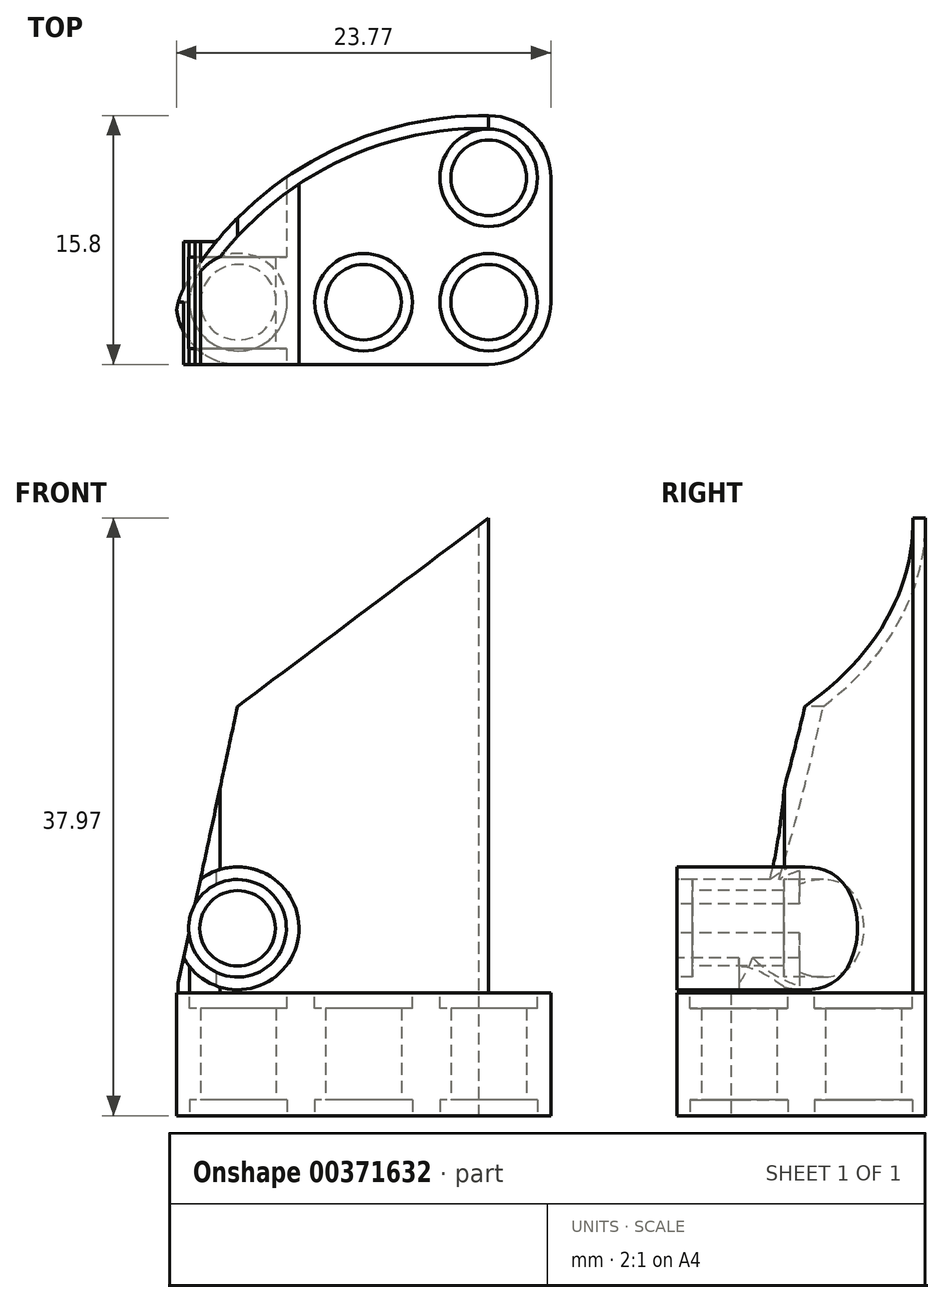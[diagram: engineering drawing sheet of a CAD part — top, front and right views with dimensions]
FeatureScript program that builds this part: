
annotation { "Feature Type Name" : "Feature", "Feature Type Description" : "" }
export const myFeature = defineFeature(function(context is Context, id is Id, definition is map)
    precondition{}
    {
        {
            var Q0;
            Q0=qCreatedBy(makeId("Top.planeOp"),FACE);
            var sketch = newSketch(context, id + "F0", { "sketchPlane" : qUnion([Q0])});
            skLineSegment(sketch, "E0", {"start": v(0, 0) * mm, "end": v(11.9, 0) * mm, "construction": true});
            skLineSegment(sketch, "E1", {"start": v(11.9, 0) * mm, "end": v(11.9, 7.9) * mm});
            skLineSegment(sketch, "E2", {"start": v(11.9, 0) * mm, "end": v(11.9, -7.9) * mm});
            skLineSegment(sketch, "E3", {"start": v(11.9, -7.9) * mm, "end": v(-11.9, -7.9) * mm});
            skLineSegment(sketch, "E4", {"start": v(-11.9, -7.9) * mm, "end": v(-11.9, 0) * mm});
            skLineSegment(sketch, "E5", {"start": v(11.9, 7.9) * mm, "end": v(4, 7.9) * mm});
            skLineSegment(sketch, "E6", {"start": v(4, 7.9) * mm, "end": v(4, 0) * mm});
            skLineSegment(sketch, "E7", {"start": v(4, 0) * mm, "end": v(-11.9, 0) * mm});
            skCircle(sketch, "E8", {"center": v(7.95, 3.95) * mm, "radius": 2.4 * mm});
            skPoint(sketch, "E8.centerSnap0", {"position": v(7.95, 7.9) * mm});
            skPoint(sketch, "E8.centerSnap1", {"position": v(11.9, 3.95) * mm});
            skCircle(sketch, "E9", {"center": v(7.95, 3.95) * mm, "radius": 3.1 * mm});
            skLineSegment(sketch, "E10", {"start": v(11.9, -7.9) * mm, "end": v(4, -7.9) * mm, "construction": true});
            skLineSegment(sketch, "E11", {"start": v(4, -7.9) * mm, "end": v(-4, -7.9) * mm, "construction": true});
            skLineSegment(sketch, "E12", {"start": v(-4, -7.9) * mm, "end": v(-11.9, -7.9) * mm, "construction": true});
            skLineSegment(sketch, "E13", {"start": v(11.9, -3.95) * mm, "end": v(-11.9, -3.95) * mm, "construction": true});
            skCircle(sketch, "E14", {"center": v(7.95, -3.95) * mm, "radius": 2.4 * mm});
            skPoint(sketch, "E14.centerSnap0", {"position": v(7.95, -7.9) * mm});
            skCircle(sketch, "E15", {"center": v(7.95, -3.95) * mm, "radius": 3.1 * mm});
            skCircle(sketch, "E16", {"center": v(0, -3.95) * mm, "radius": 2.4 * mm});
            skCircle(sketch, "E17", {"center": v(0, -3.95) * mm, "radius": 3.1 * mm});
            skCircle(sketch, "E18", {"center": v(-7.95, -3.95) * mm, "radius": 2.4 * mm});
            skPoint(sketch, "E18.centerSnap0", {"position": v(-7.95, -7.9) * mm});
            skCircle(sketch, "E19", {"center": v(-7.95, -3.95) * mm, "radius": 3.1 * mm});
            skArc(sketch, "E20", {"start": v(7.95, 7.9) * mm, "mid": v(-3.66, 4.8) * mm, "end": v(-11.9, -3.95) * mm});
            skArc(sketch, "E21.trimOffspring", {"start": v(-10.35, -3.82) * mm, "mid": v(-10.38, -3.88) * mm, "end": v(-10.42, -3.95) * mm});
            skArc(sketch, "E22.0", {"start": v(7.94, 7.1) * mm, "mid": v(-1.55, 5.02) * mm, "end": v(-9.1, -1.07) * mm});
            skLineSegment(sketch, "E23", {"start": v(7.95, 7.9) * mm, "end": v(7.94, 7.1) * mm});
            skLineSegment(sketch, "E24", {"start": v(-11.9, -3.95) * mm, "end": v(-11.05, -3.95) * mm});
            skArc(sketch, "E25.trimOffspring", {"start": v(-11, -3.95) * mm, "mid": v(-11.02, -4) * mm, "end": v(-11.05, -4.05) * mm});
            skSolve(sketch);
        }
        {
            var Q0;
            Q0=makeQuery(id+"F0.imprint","IMPRINT",FACE,{"disambiguationData":[TD([[makeQuery(id+"F0.imprint","IMPRINT",EDGE,{"derivedFrom":sQuery(id+"F0.wireOp",EDGE,"E1")}),1.0]])]});
            var Q1;
            Q1=makeQuery(id+"F0.imprint","IMPRINT",FACE,{"disambiguationData":[TD([[makeQuery(id+"F0.imprint","IMPRINT",EDGE,{"derivedFrom":sQuery(id+"F0.wireOp",EDGE,"E14")}),-1.0]])]});
            var Q2;
            Q2=makeQuery(id+"F0.imprint","IMPRINT",FACE,{"disambiguationData":[TD([[makeQuery(id+"F0.imprint","IMPRINT",EDGE,{"derivedFrom":sQuery(id+"F0.wireOp",EDGE,"E8")}),-1.0]])]});
            var Q3;
            Q3=makeQuery(id+"F0.imprint","IMPRINT",FACE,{"disambiguationData":[TD([[makeQuery(id+"F0.imprint","IMPRINT",EDGE,{"derivedFrom":sQuery(id+"F0.wireOp",EDGE,"E16")}),-1.0]])]});
            var Q4;
            Q4=makeQuery(id+"F0.imprint","IMPRINT",FACE,{"disambiguationData":[TD([[makeQuery(id+"F0.imprint","IMPRINT",EDGE,{"derivedFrom":sQuery(id+"F0.wireOp",EDGE,"E18")}),-1.0]])]});
            extrude(context, id + "F1", {"entities" : qUnion([Q0, Q1, Q2, Q3, Q4]), "depth" : 7.8 * mm});
        }
        {
            var Q0;
            Q0=makeQuery(id+"F0.imprint","IMPRINT",FACE,{"disambiguationData":[TD([[makeQuery(id+"F0.imprint","IMPRINT",EDGE,{"derivedFrom":sQuery(id+"F0.wireOp",EDGE,"E8")}),-1.0]])]});
            var Q1;
            Q1=makeQuery(id+"F0.imprint","IMPRINT",FACE,{"disambiguationData":[TD([[makeQuery(id+"F0.imprint","IMPRINT",EDGE,{"derivedFrom":sQuery(id+"F0.wireOp",EDGE,"E14")}),-1.0]])]});
            var Q2;
            Q2=makeQuery(id+"F0.imprint","IMPRINT",FACE,{"disambiguationData":[TD([[makeQuery(id+"F0.imprint","IMPRINT",EDGE,{"derivedFrom":sQuery(id+"F0.wireOp",EDGE,"E16")}),-1.0]])]});
            var Q3;
            Q3=makeQuery(id+"F0.imprint","IMPRINT",FACE,{"disambiguationData":[TD([[makeQuery(id+"F0.imprint","IMPRINT",EDGE,{"derivedFrom":sQuery(id+"F0.wireOp",EDGE,"E18")}),-1.0]])]});
            extrude(context, id + "F2", {"entities" : qUnion([Q0, Q1, Q2, Q3]), "operationType" : NewBodyOperationType.REMOVE, "depth" : 1 * mm});
        }
        {
            var Q0;
            Q0=makeQuery(id+"F1.opExtrude","CAP_FACE",FACE,{"disambiguationData":[OSD([sQuery(id+"F0.wireOp",EDGE,"E1"),sQuery(id+"F0.wireOp",EDGE,"E2"),sQuery(id+"F0.wireOp",EDGE,"E3"),sQuery(id+"F0.wireOp",EDGE,"E4"),sQuery(id+"F0.wireOp",EDGE,"E5"),sQuery(id+"F0.wireOp",EDGE,"E6"),sQuery(id+"F0.wireOp",EDGE,"E7"),sQuery(id+"F0.wireOp",EDGE,"E8"),sQuery(id+"F0.wireOp",EDGE,"E14"),sQuery(id+"F0.wireOp",EDGE,"E16"),sQuery(id+"F0.wireOp",EDGE,"E18")])],"isStart":false});
            var sketch = newSketch(context, id + "F3", { "sketchPlane" : qUnion([Q0])});
            skCircle(sketch, "E26", {"center": v(7.95, 3.95) * mm, "radius": 3.1 * mm});
            skCircle(sketch, "E27", {"center": v(7.95, -3.95) * mm, "radius": 3.1 * mm});
            skCircle(sketch, "E28", {"center": v(0, -3.95) * mm, "radius": 3.1 * mm});
            skCircle(sketch, "E29", {"center": v(-7.95, -3.95) * mm, "radius": 3.1 * mm});
            skSolve(sketch);
        }
        {
            var Q0;
            Q0=makeQuery(id+"F3.imprint","IMPRINT",FACE,{"disambiguationData":[TD([[makeQuery(id+"F3.imprint","IMPRINT",EDGE,{"derivedFrom":sQuery(id+"F3.wireOp",EDGE,"E26")}),1.0]])]});
            var Q1;
            Q1=makeQuery(id+"F3.imprint","IMPRINT",FACE,{"disambiguationData":[TD([[makeQuery(id+"F3.imprint","IMPRINT",EDGE,{"derivedFrom":sQuery(id+"F3.wireOp",EDGE,"E27")}),1.0]])]});
            var Q2;
            Q2=makeQuery(id+"F3.imprint","IMPRINT",FACE,{"disambiguationData":[TD([[makeQuery(id+"F3.imprint","IMPRINT",EDGE,{"derivedFrom":sQuery(id+"F3.wireOp",EDGE,"E28")}),1.0]])]});
            var Q3;
            Q3=makeQuery(id+"F3.imprint","IMPRINT",FACE,{"disambiguationData":[TD([[makeQuery(id+"F3.imprint","IMPRINT",EDGE,{"derivedFrom":sQuery(id+"F3.wireOp",EDGE,"E29")}),1.0]])]});
            extrude(context, id + "F4", {"entities" : qUnion([Q0, Q1, Q2, Q3]), "operationType" : NewBodyOperationType.REMOVE, "oppositeDirection" : true, "depth" : 1 * mm});
        }
        {
            var Q0;
            {var subQ5=sQuery(id+"F0.wireOp",EDGE,"E24");Q0=makeQuery(id+"F0.imprint","IMPRINT",FACE,{"disambiguationData":[TD([[makeQuery(id+"F0.imprint","IMPRINT",EDGE,{"derivedFrom":subQ5}),1.0]])]});}
            var Q1;
            {var subQ0=sQuery(id+"F0.wireOp",EDGE,"E20");var subQ1=sQuery(id+"F0.wireOp",EDGE,"E6");var subQ2=makeQuery(id+"F0.imprint","INTERSECT",VERTEX,{"derivedFrom":[subQ1,subQ0]});Q1=makeQuery(id+"F0.imprint","IMPRINT",FACE,{"disambiguationData":[TD([[makeQuery(id+"F0.imprint","IMPRINT",EDGE,{"disambiguationData":[TD([[subQ2,-1.0]])],"derivedFrom":subQ1}),-1.0]])]});}
            var Q2;
            {var subQ0=sQuery(id+"F0.wireOp",EDGE,"E23");Q2=makeQuery(id+"F0.imprint","IMPRINT",FACE,{"disambiguationData":[TD([[makeQuery(id+"F0.imprint","IMPRINT",EDGE,{"derivedFrom":subQ0}),-1.0]])]});}
            extrude(context, id + "F5", {"entities" : qUnion([Q0, Q1, Q2]), "operationType" : NewBodyOperationType.ADD, "depth" : 38 * mm});
        }
        {
            var Q0;
            {var subQ0=sQuery(id+"F0.wireOp",EDGE,"E7");var subQ1=sQuery(id+"F0.wireOp",EDGE,"E6");var subQ2=makeQuery(id+"F0.imprint","INTERSECT",VERTEX,{"derivedFrom":[subQ1,subQ0]});Q0=makeQuery(id+"F0.imprint","IMPRINT",FACE,{"disambiguationData":[TD([[makeQuery(id+"F0.imprint","IMPRINT",EDGE,{"disambiguationData":[TD([[subQ2,1.0]])],"derivedFrom":subQ1}),-1.0]])]});}
            extrude(context, id + "F6", {"entities" : qUnion([Q0]), "operationType" : NewBodyOperationType.ADD, "depth" : 7.8 * mm});
        }
        {
            var Q0;
            Q0=makeQuery(id+"F1.opExtrude","SWEPT_FACE",FACE,{"disambiguationData":[OSD([sQuery(id+"F0.wireOp",EDGE,"E3")])]});
            var sketch = newSketch(context, id + "F7", { "sketchPlane" : qUnion([Q0])});
            skLineSegment(sketch, "E30", {"start": v(-11.9, 0) * mm, "end": v(-8, 0) * mm});
            skLineSegment(sketch, "E31", {"start": v(-8, 0) * mm, "end": v(-8, 11.9) * mm});
            skLineSegment(sketch, "E32", {"start": v(-8, 0) * mm, "end": v(-8, 26) * mm, "construction": true});
            skLineSegment(sketch, "E33", {"start": v(11.9, 0) * mm, "end": v(8, 0) * mm, "construction": true});
            skLineSegment(sketch, "E34", {"start": v(8, 0) * mm, "end": v(8, 38) * mm});
            skLineSegment(sketch, "E35", {"start": v(-11.9, 7.8) * mm, "end": v(-8, 26) * mm});
            skLineSegment(sketch, "E36", {"start": v(-8, 26) * mm, "end": v(8, 38) * mm});
            skCircle(sketch, "E37", {"center": v(-8, 11.9) * mm, "radius": 2.4 * mm});
            skCircle(sketch, "E38", {"center": v(-8, 11.9) * mm, "radius": 3.1 * mm});
            skCircle(sketch, "E39", {"center": v(-8, 11.9) * mm, "radius": 3.9 * mm});
            skLineSegment(sketch, "E40", {"start": v(8, 7.8) * mm, "end": v(11.9, 7.8) * mm});
            skLineSegment(sketch, "E41", {"start": v(11.9, 7.8) * mm, "end": v(11.9, 0) * mm});
            skLineSegment(sketch, "E42", {"start": v(-11.9, 0) * mm, "end": v(-11.9, 7.8) * mm});
            skSolve(sketch);
        }
        {
            var Q0;
            Q0=makeQuery(id+"F7.imprint","IMPRINT",FACE,{"disambiguationData":[TD([[makeQuery(id+"F7.imprint","IMPRINT",EDGE,{"derivedFrom":sQuery(id+"F7.wireOp",EDGE,"E37")}),-1.0]])]});
            var Q1;
            {var subQ0=sQuery(id+"F7.wireOp",EDGE,"E38");var subQ1=sQuery(id+"F7.wireOp",EDGE,"E35");var subQ2=makeQuery(id+"F7.imprint","INTERSECT",VERTEX,{"disambiguationData":[OD(0.0)],"derivedFrom":[subQ1,subQ0]});Q1=makeQuery(id+"F7.imprint","IMPRINT",FACE,{"disambiguationData":[TD([[makeQuery(id+"F7.imprint","IMPRINT",EDGE,{"disambiguationData":[TD([[subQ2,-1.0]])],"derivedFrom":subQ1}),1.0]])]});}
            extrude(context, id + "F8", {"entities" : qUnion([Q0, Q1]), "operationType" : NewBodyOperationType.REMOVE, "oppositeDirection" : true, "depth" : 25 * mm});
        }
        {
            var Q0;
            {var subQ0=sQuery(id+"F7.wireOp",EDGE,"E39");var subQ1=sQuery(id+"F7.wireOp",EDGE,"E35");var subQ2=makeQuery(id+"F7.imprint","INTERSECT",VERTEX,{"disambiguationData":[OD(1.0)],"derivedFrom":[subQ1,subQ0]});Q0=makeQuery(id+"F7.imprint","IMPRINT",FACE,{"disambiguationData":[TD([[makeQuery(id+"F7.imprint","IMPRINT",EDGE,{"disambiguationData":[TD([[subQ2,-1.0]])],"derivedFrom":subQ1}),1.0]])]});}
            var Q1;
            {var subQ0=sQuery(id+"F7.wireOp",EDGE,"E39");var subQ1=sQuery(id+"F7.wireOp",EDGE,"E31");var subQ2=makeQuery(id+"F7.imprint","INTERSECT",VERTEX,{"derivedFrom":[subQ1,subQ0]});Q1=makeQuery(id+"F7.imprint","IMPRINT",FACE,{"disambiguationData":[TD([[makeQuery(id+"F7.imprint","IMPRINT",EDGE,{"disambiguationData":[TD([[subQ2,-1.0]])],"derivedFrom":subQ1}),1.0]])]});}
            var Q2;
            {var subQ0=sQuery(id+"F7.wireOp",EDGE,"E39");var subQ1=sQuery(id+"F7.wireOp",EDGE,"E31");var subQ2=makeQuery(id+"F7.imprint","INTERSECT",VERTEX,{"derivedFrom":[subQ1,subQ0]});Q2=makeQuery(id+"F7.imprint","IMPRINT",FACE,{"disambiguationData":[TD([[makeQuery(id+"F7.imprint","IMPRINT",EDGE,{"disambiguationData":[TD([[subQ2,-1.0]])],"derivedFrom":subQ1}),-1.0]])]});}
            var Q3;
            {var subQ0=sQuery(id+"F7.wireOp",EDGE,"E39");var subQ1=sQuery(id+"F7.wireOp",EDGE,"E35");var subQ2=makeQuery(id+"F7.imprint","INTERSECT",VERTEX,{"disambiguationData":[OD(0.0)],"derivedFrom":[subQ1,subQ0]});Q3=makeQuery(id+"F7.imprint","IMPRINT",FACE,{"disambiguationData":[TD([[makeQuery(id+"F7.imprint","IMPRINT",EDGE,{"disambiguationData":[TD([[subQ2,-1.0]])],"derivedFrom":subQ1}),1.0]])]});}
            var Q4;
            {var subQ0=sQuery(id+"F7.wireOp",EDGE,"E38");var subQ1=sQuery(id+"F7.wireOp",EDGE,"E35");var subQ2=makeQuery(id+"F7.imprint","INTERSECT",VERTEX,{"disambiguationData":[OD(0.0)],"derivedFrom":[subQ1,subQ0]});Q4=makeQuery(id+"F7.imprint","IMPRINT",FACE,{"disambiguationData":[TD([[makeQuery(id+"F7.imprint","IMPRINT",EDGE,{"disambiguationData":[TD([[subQ2,-1.0]])],"derivedFrom":subQ1}),1.0]])]});}
            var Q5;
            Q5=makeQuery(id+"F7.imprint","IMPRINT",FACE,{"disambiguationData":[TD([[makeQuery(id+"F7.imprint","IMPRINT",EDGE,{"derivedFrom":sQuery(id+"F7.wireOp",EDGE,"E37")}),-1.0]])]});
            extrude(context, id + "F9", {"entities" : qUnion([Q0, Q1, Q2, Q3, Q4, Q5]), "operationType" : NewBodyOperationType.ADD, "oppositeDirection" : true, "depth" : 7.8 * mm});
        }
        {
            var Q0;
            Q0=makeQuery(id+"F7.imprint","IMPRINT",FACE,{"disambiguationData":[TD([[makeQuery(id+"F7.imprint","IMPRINT",EDGE,{"derivedFrom":sQuery(id+"F7.wireOp",EDGE,"E37")}),1.0]])]});
            extrude(context, id + "F10", {"entities" : qUnion([Q0]), "operationType" : NewBodyOperationType.REMOVE, "oppositeDirection" : true, "depth" : 25 * mm});
        }
        {
            var Q0;
            Q0=makeQuery(id+"F7.imprint","IMPRINT",FACE,{"disambiguationData":[TD([[makeQuery(id+"F7.imprint","IMPRINT",EDGE,{"derivedFrom":sQuery(id+"F7.wireOp",EDGE,"E37")}),-1.0]])]});
            var Q1;
            {var subQ0=sQuery(id+"F7.wireOp",EDGE,"E38");var subQ1=sQuery(id+"F7.wireOp",EDGE,"E35");var subQ2=makeQuery(id+"F7.imprint","INTERSECT",VERTEX,{"disambiguationData":[OD(0.0)],"derivedFrom":[subQ1,subQ0]});Q1=makeQuery(id+"F7.imprint","IMPRINT",FACE,{"disambiguationData":[TD([[makeQuery(id+"F7.imprint","IMPRINT",EDGE,{"disambiguationData":[TD([[subQ2,-1.0]])],"derivedFrom":subQ1}),1.0]])]});}
            extrude(context, id + "F11", {"entities" : qUnion([Q0, Q1]), "operationType" : NewBodyOperationType.REMOVE, "oppositeDirection" : true, "depth" : 1 * mm});
        }
        {
            var Q0;
            {var subQ0=sQuery(id+"F7.wireOp",EDGE,"E36");Q0=makeQuery(id+"F7.imprint","IMPRINT",FACE,{"disambiguationData":[TD([[makeQuery(id+"F7.imprint","IMPRINT",EDGE,{"derivedFrom":subQ0}),-1.0]])]});}
            var Q1;
            {var subQ0=sQuery(id+"F7.wireOp",EDGE,"E39");var subQ1=sQuery(id+"F7.wireOp",EDGE,"E31");var subQ2=makeQuery(id+"F7.imprint","INTERSECT",VERTEX,{"derivedFrom":[subQ1,subQ0]});Q1=makeQuery(id+"F7.imprint","IMPRINT",FACE,{"disambiguationData":[TD([[makeQuery(id+"F7.imprint","IMPRINT",EDGE,{"disambiguationData":[TD([[subQ2,1.0]])],"derivedFrom":subQ1}),1.0]])]});}
            var Q2;
            {var subQ0=sQuery(id+"F7.wireOp",EDGE,"E38");var subQ1=sQuery(id+"F7.wireOp",EDGE,"E31");var subQ2=makeQuery(id+"F7.imprint","INTERSECT",VERTEX,{"derivedFrom":[subQ1,subQ0]});Q2=makeQuery(id+"F7.imprint","IMPRINT",FACE,{"disambiguationData":[TD([[makeQuery(id+"F7.imprint","IMPRINT",EDGE,{"disambiguationData":[TD([[subQ2,1.0]])],"derivedFrom":subQ1}),-1.0]])]});}
            var Q3;
            Q3=makeQuery(id+"F7.imprint","IMPRINT",FACE,{"disambiguationData":[TD([[makeQuery(id+"F7.imprint","IMPRINT",EDGE,{"derivedFrom":sQuery(id+"F7.wireOp",EDGE,"E37")}),-1.0]])]});
            var Q4;
            {var subQ0=sQuery(id+"F7.wireOp",EDGE,"E38");var subQ1=sQuery(id+"F7.wireOp",EDGE,"E31");var subQ2=makeQuery(id+"F7.imprint","INTERSECT",VERTEX,{"derivedFrom":[subQ1,subQ0]});Q4=makeQuery(id+"F7.imprint","IMPRINT",FACE,{"disambiguationData":[TD([[makeQuery(id+"F7.imprint","IMPRINT",EDGE,{"disambiguationData":[TD([[subQ2,1.0]])],"derivedFrom":subQ1}),1.0]])]});}
            var Q5;
            {var subQ0=sQuery(id+"F7.wireOp",EDGE,"E31");var subQ1=sQuery(id+"F0.wireOp",EDGE,"E3");var subQ4=makeQuery(id+"F1.opExtrude","CAP_EDGE",EDGE,{"disambiguationData":[OSD([subQ1])],"isStart":false});var subQ5=makeQuery(id+"F7.imprint","INTERSECT",VERTEX,{"derivedFrom":[subQ4,subQ0]});Q5=makeQuery(id+"F7.imprint","IMPRINT",FACE,{"disambiguationData":[TD([[makeQuery(id+"F7.imprint","IMPRINT",EDGE,{"disambiguationData":[TD([[subQ5,1.0]])],"derivedFrom":subQ0}),-1.0]])]});}
            var Q6;
            {var subQ0=sQuery(id+"F7.wireOp",EDGE,"E30");Q6=makeQuery(id+"F7.imprint","IMPRINT",FACE,{"disambiguationData":[TD([[makeQuery(id+"F7.imprint","IMPRINT",EDGE,{"derivedFrom":subQ0}),-1.0]])]});}
            var Q7;
            {var subQ4=sQuery(id+"F7.wireOp",EDGE,"E40");Q7=makeQuery(id+"F7.imprint","IMPRINT",FACE,{"disambiguationData":[TD([[makeQuery(id+"F7.imprint","IMPRINT",EDGE,{"derivedFrom":subQ4}),1.0]])]});}
            var Q8;
            {var subQ0=sQuery(id+"F7.wireOp",EDGE,"E39");var subQ1=sQuery(id+"F7.wireOp",EDGE,"E35");var subQ2=makeQuery(id+"F7.imprint","INTERSECT",VERTEX,{"disambiguationData":[OD(0.0)],"derivedFrom":[subQ1,subQ0]});Q8=makeQuery(id+"F7.imprint","IMPRINT",FACE,{"disambiguationData":[TD([[makeQuery(id+"F7.imprint","IMPRINT",EDGE,{"disambiguationData":[TD([[subQ2,-1.0]])],"derivedFrom":subQ1}),1.0]])]});}
            var Q9;
            {var subQ0=sQuery(id+"F7.wireOp",EDGE,"E38");var subQ1=sQuery(id+"F7.wireOp",EDGE,"E35");var subQ2=makeQuery(id+"F7.imprint","INTERSECT",VERTEX,{"disambiguationData":[OD(0.0)],"derivedFrom":[subQ1,subQ0]});Q9=makeQuery(id+"F7.imprint","IMPRINT",FACE,{"disambiguationData":[TD([[makeQuery(id+"F7.imprint","IMPRINT",EDGE,{"disambiguationData":[TD([[subQ2,-1.0]])],"derivedFrom":subQ1}),1.0]])]});}
            extrude(context, id + "F12", {"entities" : qUnion([Q0, Q1, Q2, Q3, Q4, Q5, Q6, Q7, Q8, Q9]), "operationType" : NewBodyOperationType.INTERSECT, "oppositeDirection" : true, "depth" : 25 * mm});
        }
        {
            var Q0;
            Q0=makeQuery(id+"F9.opExtrude","CAP_FACE",FACE,{"disambiguationData":[OSD([sQuery(id+"F7.wireOp",EDGE,"E37"),sQuery(id+"F7.wireOp",EDGE,"E39")])],"isStart":false});
            var sketch = newSketch(context, id + "F13", { "sketchPlane" : qUnion([Q0])});
            skCircle(sketch, "E43", {"center": v(8, 11.9) * mm, "radius": 3.1 * mm});
            skSolve(sketch);
        }
        {
            var Q0;
            {var subQ1=sQuery(id+"F7.wireOp",EDGE,"E37");var subQ2=makeQuery(id+"F9.opExtrude","CAP_FACE",FACE,{"disambiguationData":[OSD([subQ1,sQuery(id+"F7.wireOp",EDGE,"E39")])],"isStart":false});var subQ6=sQuery(id+"F0.wireOp",EDGE,"E22.0");var subQ7=sQuery(id+"F0.wireOp",EDGE,"E20");var subQ23=makeQuery(id+"F5.opExtrude","SWEPT_FACE",FACE,{"disambiguationData":[OSD([subQ6])]});var subQ26=makeQuery(id+"F5.opExtrude","SWEPT_FACE",FACE,{"disambiguationData":[OSD([subQ7])]});var subQ31=makeQuery(id+"F8.boolean.opBoolean","COPY",FACE,{"derivedFrom":makeQuery(id+"F8.opExtrude","SWEPT_FACE",FACE,{"disambiguationData":[OSD([subQ1])]})});var subQ32=makeQuery(id+"F9.opExtrude","CAP_EDGE",EDGE,{"disambiguationData":[OSD([subQ1])],"isStart":false});var subQ33=makeQuery(id+"F9.opExtrude","SWEPT_FACE",FACE,{"disambiguationData":[OSD([subQ1])]});Q0=makeQuery(id+"F13.imprint","IMPRINT",FACE,{"disambiguationData":[TD([[makeQuery(id+"F13.imprint","IMPRINT",EDGE,{"derivedFrom":makeQuery(id+"F10.boolean.opBoolean","MERGE",EDGE,{"derivedFrom":[makeQuery(id+"F9.boolean.opBoolean","SPLIT",EDGE,{"disambiguationData":[topologyDisambiguationEdgeConnected([subQ33,subQ2]),TD([subQ26])],"derivedFrom":subQ32}),makeQuery(id+"F9.boolean.opBoolean","SPLIT",EDGE,{"disambiguationData":[topologyDisambiguationEdgeConnected([subQ33,subQ2]),TD([subQ23])],"derivedFrom":subQ32}),makeQuery(id+"F9.boolean.opBoolean","SPLIT",EDGE,{"disambiguationData":[topologyDisambiguationEdgeConnected([subQ31,subQ2]),OD(0.0)],"derivedFrom":subQ32}),makeQuery(id+"F9.boolean.opBoolean","SPLIT",EDGE,{"disambiguationData":[topologyDisambiguationEdgeConnected([subQ31,subQ2]),OD(1.0)],"derivedFrom":subQ32})]})}),1.0]])]});}
            extrude(context, id + "F14", {"entities" : qUnion([Q0]), "operationType" : NewBodyOperationType.REMOVE, "oppositeDirection" : true, "depth" : 1 * mm});
        }
        {
            var Q0;
            {var subQ0=sQuery(id+"F7.wireOp",EDGE,"E39");Q0=makeQuery(id+"F14.boolean.opBoolean","SPLIT",FACE,{"disambiguationData":[TD([makeQuery(id+"F5.opExtrude","SWEPT_FACE",FACE,{"disambiguationData":[OSD([sQuery(id+"F0.wireOp",EDGE,"E22.0")])]})])],"derivedFrom":makeQuery(id+"F9.opExtrude","CAP_FACE",FACE,{"disambiguationData":[OSD([sQuery(id+"F7.wireOp",EDGE,"E37"),subQ0])],"isStart":false})});}
            extrude(context, id + "F15", {"entities" : qUnion([Q0]), "operationType" : NewBodyOperationType.ADD, "endBound" : BoundingType.UP_TO_NEXT, "depth" : 25 * mm});
        }
        {
            var Q0;
            Q0=makeQuery(id+"F1.opExtrude","SWEPT_EDGE",EDGE,{"disambiguationData":[OSD([sQuery(id+"F0.wireOp",EDGE,"E1"),sQuery(id+"F0.wireOp",EDGE,"E5")])]});
            var Q1;
            Q1=makeQuery(id+"F1.opExtrude","SWEPT_EDGE",EDGE,{"disambiguationData":[OSD([sQuery(id+"F0.wireOp",EDGE,"E5"),sQuery(id+"F0.wireOp",EDGE,"E20")])]});
            var Q2;
            Q2=makeQuery(id+"F1.opExtrude","SWEPT_EDGE",EDGE,{"disambiguationData":[OSD([sQuery(id+"F0.wireOp",EDGE,"E3"),sQuery(id+"F0.wireOp",EDGE,"E4")])]});
            var Q3;
            Q3=makeQuery(id+"F1.opExtrude","SWEPT_EDGE",EDGE,{"disambiguationData":[OSD([sQuery(id+"F0.wireOp",EDGE,"E3"),sQuery(id+"F0.wireOp",EDGE,"E4")])]});
            var Q4;
            Q4=makeQuery(id+"F1.opExtrude","SWEPT_EDGE",EDGE,{"disambiguationData":[OSD([sQuery(id+"F0.wireOp",EDGE,"E4"),sQuery(id+"F0.wireOp",EDGE,"E20")])]});
            var Q5;
            Q5=makeQuery(id+"F1.opExtrude","SWEPT_EDGE",EDGE,{"disambiguationData":[OSD([sQuery(id+"F0.wireOp",EDGE,"E1"),sQuery(id+"F0.wireOp",EDGE,"E5")])]});
            var Q6;
            Q6=makeQuery(id+"F1.opExtrude","SWEPT_EDGE",EDGE,{"disambiguationData":[OSD([sQuery(id+"F0.wireOp",EDGE,"E2"),sQuery(id+"F0.wireOp",EDGE,"E3")])]});
            fillet(context, id + "F16", {"entities" : qUnion([Q0, Q1, Q2, Q3, Q4, Q5, Q6]), "radius" : (7.9 / 2) * mm, "tangentPropagation" : true, "allowEdgeOverflow" : false});
        }
    });
